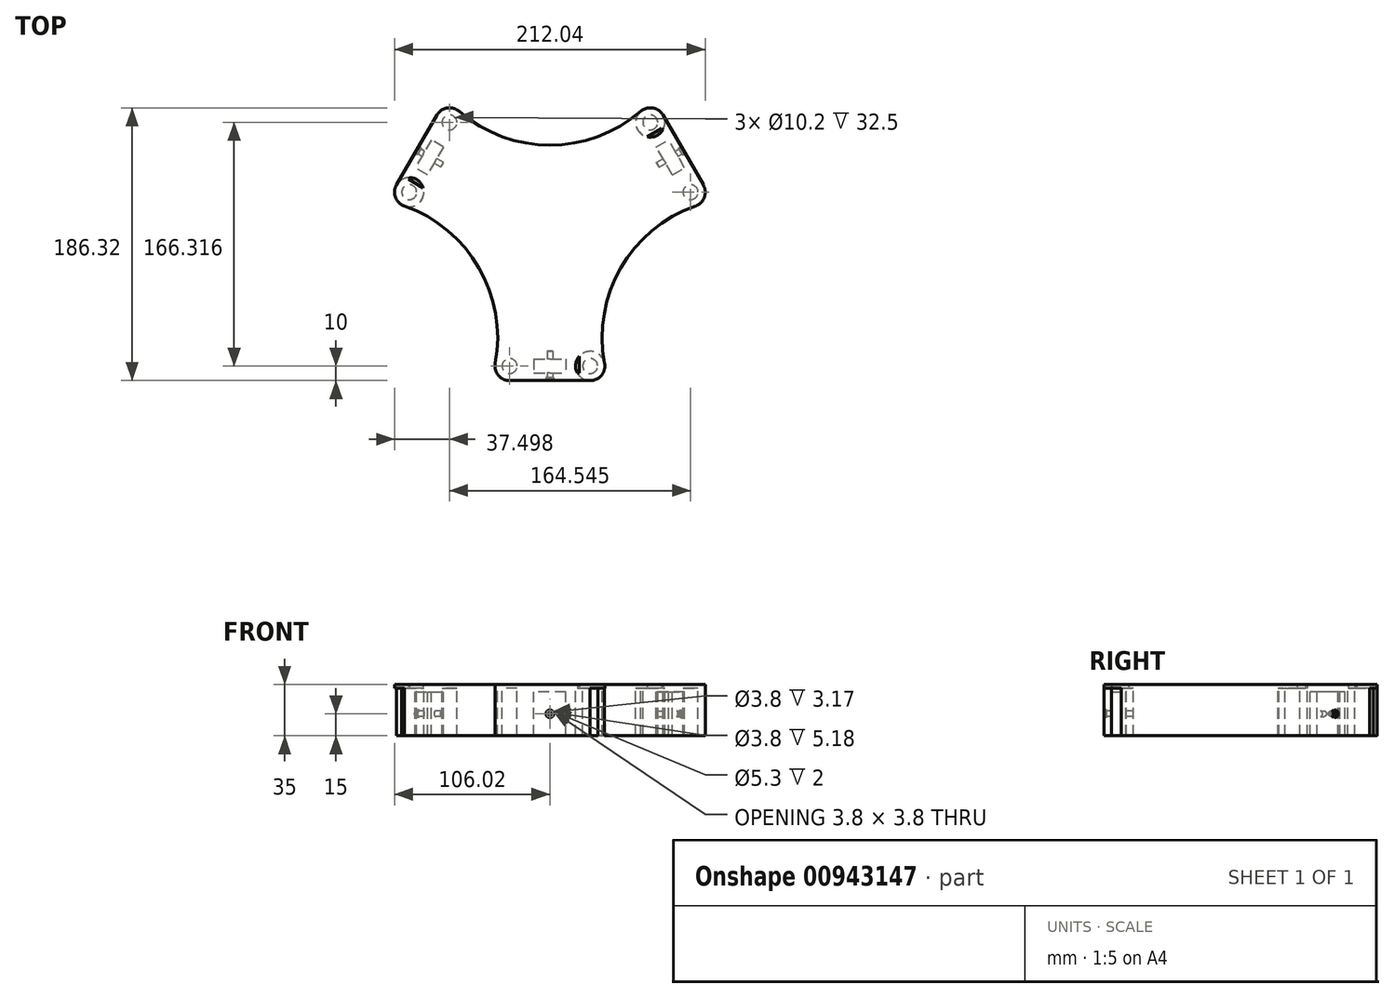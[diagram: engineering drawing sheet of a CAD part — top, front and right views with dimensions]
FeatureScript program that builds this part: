
annotation { "Feature Type Name" : "Feature", "Feature Type Description" : "" }
export const myFeature = defineFeature(function(context is Context, id is Id, definition is map)
    precondition{}
    {
        {
            var Q0;
            Q0=qCreatedBy(makeId("Top.planeOp"),FACE);
            var sketch = newSketch(context, id + "F0", { "sketchPlane" : qUnion([Q0])});
            skCircle(sketch, "E0", {"center": v(0, 0) * mm, "radius": 57.15 * mm, "construction": true});
            skLineSegment(sketch, "E1.bottom", {"start": v(110, 110) * mm, "end": v(-110, 110) * mm, "construction": true});
            skLineSegment(sketch, "E1.top", {"start": v(110, -110) * mm, "end": v(-110, -110) * mm, "construction": true});
            skLineSegment(sketch, "E1.left", {"start": v(110, 110) * mm, "end": v(110, -110) * mm, "construction": true});
            skLineSegment(sketch, "E1.right", {"start": v(-110, 110) * mm, "end": v(-110, -110) * mm, "construction": true});
            skLineSegment(sketch, "E2", {"start": v(0, 0) * mm, "end": v(0, -95) * mm});
            skLineSegment(sketch, "E3", {"start": v(0, 0) * mm, "end": v(-78.54, -45.35) * mm});
            skLineSegment(sketch, "E4", {"start": v(0, 0) * mm, "end": v(-88.28, 50.97) * mm});
            skLineSegment(sketch, "E5.MirrorCS", {"start": v(0, 0) * mm, "end": v(78.54, -45.35) * mm});
            skLineSegment(sketch, "E6.MirrorCS", {"start": v(0, 0) * mm, "end": v(88.28, 50.97) * mm});
            skCircle(sketch, "E7", {"center": v(-27.5, -95) * mm, "radius": 5.1 * mm});
            skCircle(sketch, "E8", {"center": v(-27.5, -95) * mm, "radius": 10 * mm});
            skCircle(sketch, "E9.MirrorC", {"center": v(27.5, -95) * mm, "radius": 5.1 * mm});
            skCircle(sketch, "E10.MirrorC", {"center": v(27.5, -95) * mm, "radius": 10 * mm});
            skLineSegment(sketch, "E11", {"start": v(-27.5, -105) * mm, "end": v(27.5, -105) * mm});
            skCircle(sketch, "E12.1.0", {"center": v(96.02, 23.68) * mm, "radius": 10 * mm});
            skCircle(sketch, "E12.1.1", {"center": v(96.02, 23.68) * mm, "radius": 5.1 * mm});
            skLineSegment(sketch, "E12.1.2", {"start": v(104.68, 28.68) * mm, "end": v(77.18, 76.32) * mm});
            skCircle(sketch, "E12.1.3", {"center": v(68.52, 71.32) * mm, "radius": 5.1 * mm});
            skCircle(sketch, "E12.1.4", {"center": v(68.52, 71.32) * mm, "radius": 10 * mm});
            skCircle(sketch, "E12.2.0", {"center": v(-68.52, 71.32) * mm, "radius": 10 * mm});
            skCircle(sketch, "E12.2.1", {"center": v(-68.52, 71.32) * mm, "radius": 5.1 * mm});
            skLineSegment(sketch, "E12.2.2", {"start": v(-77.18, 76.32) * mm, "end": v(-104.68, 28.68) * mm});
            skCircle(sketch, "E12.2.3", {"center": v(-96.02, 23.68) * mm, "radius": 5.1 * mm});
            skCircle(sketch, "E12.2.4", {"center": v(-96.02, 23.68) * mm, "radius": 10 * mm});
            skArc(sketch, "E13", {"start": v(99.32, 14.24) * mm, "mid": v(48.39, -27.94) * mm, "end": v(37.32, -93.14) * mm});
            skArc(sketch, "E14.1.0", {"start": v(-62, 78.9) * mm, "mid": v(0, 55.87) * mm, "end": v(62, 78.9) * mm});
            skArc(sketch, "E14.2.0", {"start": v(-37.32, -93.14) * mm, "mid": v(-48.39, -27.94) * mm, "end": v(-99.32, 14.24) * mm});
            skSolve(sketch);
        }
        {
            var Q0;
            {var subQ0=sQuery(id+"F0.wireOp",EDGE,"E11");Q0=makeQuery(id+"F0.imprint","IMPRINT",FACE,{"disambiguationData":[TD([[makeQuery(id+"F0.imprint","IMPRINT",EDGE,{"derivedFrom":subQ0}),1.0]])]});}
            var Q1;
            Q1=makeQuery(id+"F0.imprint","IMPRINT",FACE,{"disambiguationData":[TD([[makeQuery(id+"F0.imprint","IMPRINT",EDGE,{"derivedFrom":sQuery(id+"F0.wireOp",EDGE,"E7")}),-1.0]])]});
            var Q2;
            Q2=makeQuery(id+"F0.imprint","IMPRINT",FACE,{"disambiguationData":[TD([[makeQuery(id+"F0.imprint","IMPRINT",EDGE,{"derivedFrom":sQuery(id+"F0.wireOp",EDGE,"E9.MirrorC")}),1.0]])]});
            extrude(context, id + "F1", {"entities" : qUnion([Q0, Q1, Q2]), "oppositeDirection" : true, "depth" : 35 * mm, "offsetDistance" : 25 * mm});
        }
        {
            var Q0;
            Q0=makeQuery(id+"F1.opExtrude","CAP_FACE",FACE,{"disambiguationData":[OSD([sQuery(id+"F0.wireOp",EDGE,"E3"),sQuery(id+"F0.wireOp",EDGE,"E5.MirrorCS"),sQuery(id+"F0.wireOp",EDGE,"E7"),sQuery(id+"F0.wireOp",EDGE,"E8"),sQuery(id+"F0.wireOp",EDGE,"E9.MirrorC"),sQuery(id+"F0.wireOp",EDGE,"E10.MirrorC"),sQuery(id+"F0.wireOp",EDGE,"E11"),sQuery(id+"F0.wireOp",EDGE,"E13"),sQuery(id+"F0.wireOp",EDGE,"E14.2.0")])],"isStart":true});
            var sketch = newSketch(context, id + "F2", { "sketchPlane" : qUnion([Q0])});
            skLineSegment(sketch, "E15.bottom", {"start": v(11, -99.83) * mm, "end": v(-11, -99.83) * mm});
            skLineSegment(sketch, "E15.top", {"start": v(11, -90.18) * mm, "end": v(-11, -90.18) * mm});
            skLineSegment(sketch, "E15.left", {"start": v(11, -99.83) * mm, "end": v(11, -90.18) * mm});
            skLineSegment(sketch, "E15.right", {"start": v(-11, -99.83) * mm, "end": v(-11, -90.18) * mm});
            skPoint(sketch, "E15.middle", {"position": v(0, -95) * mm});
            skPoint(sketch, "E15.middle.positionSnap0", {"position": v(0, -105) * mm});
            skPoint(sketch, "E15.centerSnap0", {"position": v(0, -105) * mm});
            skSolve(sketch);
        }
        {
            var Q0;
            Q0=makeQuery(id+"F2.imprint","IMPRINT",FACE,{"disambiguationData":[TD([[makeQuery(id+"F2.imprint","IMPRINT",EDGE,{"derivedFrom":sQuery(id+"F2.wireOp",EDGE,"E15.bottom")}),-1.0]])]});
            var Q1;
            Q1=makeQuery(id+"F1.opExtrude","CAP_FACE",FACE,{"disambiguationData":[OSD([sQuery(id+"F0.wireOp",EDGE,"E3"),sQuery(id+"F0.wireOp",EDGE,"E5.MirrorCS"),sQuery(id+"F0.wireOp",EDGE,"E7"),sQuery(id+"F0.wireOp",EDGE,"E8"),sQuery(id+"F0.wireOp",EDGE,"E9.MirrorC"),sQuery(id+"F0.wireOp",EDGE,"E10.MirrorC"),sQuery(id+"F0.wireOp",EDGE,"E11"),sQuery(id+"F0.wireOp",EDGE,"E13"),sQuery(id+"F0.wireOp",EDGE,"E14.2.0")])],"isStart":false});
            extrude(context, id + "F3", {"entities" : qUnion([Q0]), "operationType" : NewBodyOperationType.REMOVE, "endBound" : BoundingType.UP_TO_SURFACE, "oppositeDirection" : true, "depth" : 25 * mm, "endBoundEntityFace" : qUnion([Q1]), "offsetDistance" : 25 * mm, "hasSecondDirection" : true, "secondDirectionOppositeDirection" : true, "secondDirectionDepth" : 5 * mm});
        }
        {
            var Q0;
            Q0=makeQuery(id+"F0.imprint","IMPRINT",FACE,{"disambiguationData":[TD([[makeQuery(id+"F0.imprint","IMPRINT",EDGE,{"derivedFrom":sQuery(id+"F0.wireOp",EDGE,"E7")}),1.0]])]});
            var Q1;
            Q1=makeQuery(id+"F0.imprint","IMPRINT",FACE,{"disambiguationData":[TD([[makeQuery(id+"F0.imprint","IMPRINT",EDGE,{"derivedFrom":sQuery(id+"F0.wireOp",EDGE,"E9.MirrorC")}),-1.0]])]});
            extrude(context, id + "F4", {"entities" : qUnion([Q0, Q1]), "operationType" : NewBodyOperationType.ADD, "oppositeDirection" : true, "depth" : 2.5 * mm, "offsetDistance" : 25 * mm});
        }
        {
            var Q0;
            Q0=makeQuery(id+"F1.opExtrude","SWEPT_FACE",FACE,{"disambiguationData":[OSD([sQuery(id+"F0.wireOp",EDGE,"E11")])]});
            var sketch = newSketch(context, id + "F5", { "sketchPlane" : qUnion([Q0])});
            skLineSegment(sketch, "E16.0", {"start": v(-27.5, 0) * mm, "end": v(27.5, 0) * mm});
            skLineSegment(sketch, "E17.0", {"start": v(-27.5, -35) * mm, "end": v(27.5, -35) * mm});
            skLineSegment(sketch, "E18", {"start": v(0, 0) * mm, "end": v(0, -35) * mm, "construction": true});
            skPoint(sketch, "E19", {"position": v(0, -17.5) * mm});
            skCircle(sketch, "E20", {"center": v(0, -20) * mm, "radius": 4.15 * mm});
            skCircle(sketch, "E21", {"center": v(0, -20) * mm, "radius": 2.65 * mm});
            skCircle(sketch, "E22", {"center": v(0, -20) * mm, "radius": 1.9 * mm});
            skSolve(sketch);
        }
        {
            var Q0;
            Q0=makeQuery(id+"F5.imprint","IMPRINT",FACE,{"disambiguationData":[TD([[makeQuery(id+"F5.imprint","IMPRINT",EDGE,{"derivedFrom":sQuery(id+"F5.wireOp",EDGE,"E22")}),1.0]])]});
            extrude(context, id + "F6", {"entities" : qUnion([Q0]), "operationType" : NewBodyOperationType.REMOVE, "oppositeDirection" : true, "depth" : 20 * mm, "offsetDistance" : 25 * mm});
        }
        {
            var Q0;
            Q0=makeQuery(id+"F5.imprint","IMPRINT",FACE,{"disambiguationData":[TD([[makeQuery(id+"F5.imprint","IMPRINT",EDGE,{"derivedFrom":sQuery(id+"F5.wireOp",EDGE,"E21")}),1.0]])]});
            extrude(context, id + "F7", {"entities" : qUnion([Q0]), "operationType" : NewBodyOperationType.REMOVE, "oppositeDirection" : true, "depth" : 2 * mm, "offsetDistance" : 25 * mm});
        }
        {
            var Q0;
            Q0=makeQuery(id+"F1.opExtrude","CAP_FACE",FACE,{"disambiguationData":[OSD([sQuery(id+"F0.wireOp",EDGE,"E3"),sQuery(id+"F0.wireOp",EDGE,"E5.MirrorCS"),sQuery(id+"F0.wireOp",EDGE,"E7"),sQuery(id+"F0.wireOp",EDGE,"E8"),sQuery(id+"F0.wireOp",EDGE,"E9.MirrorC"),sQuery(id+"F0.wireOp",EDGE,"E10.MirrorC"),sQuery(id+"F0.wireOp",EDGE,"E11"),sQuery(id+"F0.wireOp",EDGE,"E13"),sQuery(id+"F0.wireOp",EDGE,"E14.2.0")])],"isStart":false});
            var sketch = newSketch(context, id + "F8", { "sketchPlane" : qUnion([Q0])});
            skLineSegment(sketch, "E23.bottom", {"start": v(20.1, 99.83) * mm, "end": v(13.3, 99.83) * mm});
            skLineSegment(sketch, "E23.top", {"start": v(20.1, 79.43) * mm, "end": v(13.3, 79.43) * mm});
            skLineSegment(sketch, "E23.left", {"start": v(20.1, 99.83) * mm, "end": v(20.1, 79.43) * mm});
            skLineSegment(sketch, "E23.right", {"start": v(13.3, 99.83) * mm, "end": v(13.3, 79.43) * mm});
            skPoint(sketch, "E23.middle", {"position": v(16.7, 89.63) * mm});
            skLineSegment(sketch, "E24", {"start": v(11, 95) * mm, "end": v(13.3, 95) * mm});
            skLineSegment(sketch, "E25", {"start": v(20.1, 95) * mm, "end": v(22.4, 95) * mm});
            skSolve(sketch);
        }
        {
            var Q0;
            {var subQ3=sQuery(id+"F8.wireOp",EDGE,"E23.bottom");Q0=makeQuery(id+"F8.imprint","IMPRINT",FACE,{"disambiguationData":[TD([[makeQuery(id+"F8.imprint","IMPRINT",EDGE,{"derivedFrom":subQ3}),1.0]])]});}
            var Q1;
            {var subQ0=sQuery(id+"F0.wireOp",EDGE,"E9.MirrorC");var subQ1=sQuery(id+"F0.wireOp",EDGE,"E7");Q1=makeQuery(id+"F4.boolean.opBoolean","MERGE",FACE,{"derivedFrom":[makeQuery(id+"F1.opExtrude","CAP_FACE",FACE,{"disambiguationData":[OSD([sQuery(id+"F0.wireOp",EDGE,"E3"),sQuery(id+"F0.wireOp",EDGE,"E5.MirrorCS"),subQ1,sQuery(id+"F0.wireOp",EDGE,"E8"),subQ0,sQuery(id+"F0.wireOp",EDGE,"E10.MirrorC"),sQuery(id+"F0.wireOp",EDGE,"E11"),sQuery(id+"F0.wireOp",EDGE,"E13"),sQuery(id+"F0.wireOp",EDGE,"E14.2.0")])],"isStart":true}),makeQuery(id+"F4.opExtrude","CAP_FACE",FACE,{"disambiguationData":[OSD([subQ1])],"isStart":true}),makeQuery(id+"F4.opExtrude","CAP_FACE",FACE,{"disambiguationData":[OSD([subQ0])],"isStart":true})]});}
            extrude(context, id + "F9", {"entities" : qUnion([Q0]), "operationType" : NewBodyOperationType.REMOVE, "endBound" : BoundingType.UP_TO_SURFACE, "oppositeDirection" : true, "depth" : 25 * mm, "endBoundEntityFace" : qUnion([Q1]), "offsetDistance" : 25 * mm});
        }
        {
            var Q0;
            Q0=makeQuery(id+"F1.opExtrude","SWEPT_BODY",BODY,{"disambiguationData":[OSD([sQuery(id+"F0.wireOp",EDGE,"E3"),sQuery(id+"F0.wireOp",EDGE,"E5.MirrorCS"),sQuery(id+"F0.wireOp",EDGE,"E7"),sQuery(id+"F0.wireOp",EDGE,"E8"),sQuery(id+"F0.wireOp",EDGE,"E9.MirrorC"),sQuery(id+"F0.wireOp",EDGE,"E10.MirrorC"),sQuery(id+"F0.wireOp",EDGE,"E11"),sQuery(id+"F0.wireOp",EDGE,"E13"),sQuery(id+"F0.wireOp",EDGE,"E14.2.0")])]});
            var Q1;
            Q1=sQuery(id+"F0.wireOp",EDGE,"E0");
            circularPattern(context, id + "F10", {"operationType" : NewBodyOperationType.ADD, "entities" : qUnion([Q0]), "axis" : qUnion([Q1]), "angle" : 240 * degree, "instanceCount" : 3, "equalSpace" : true});
        }
    });
